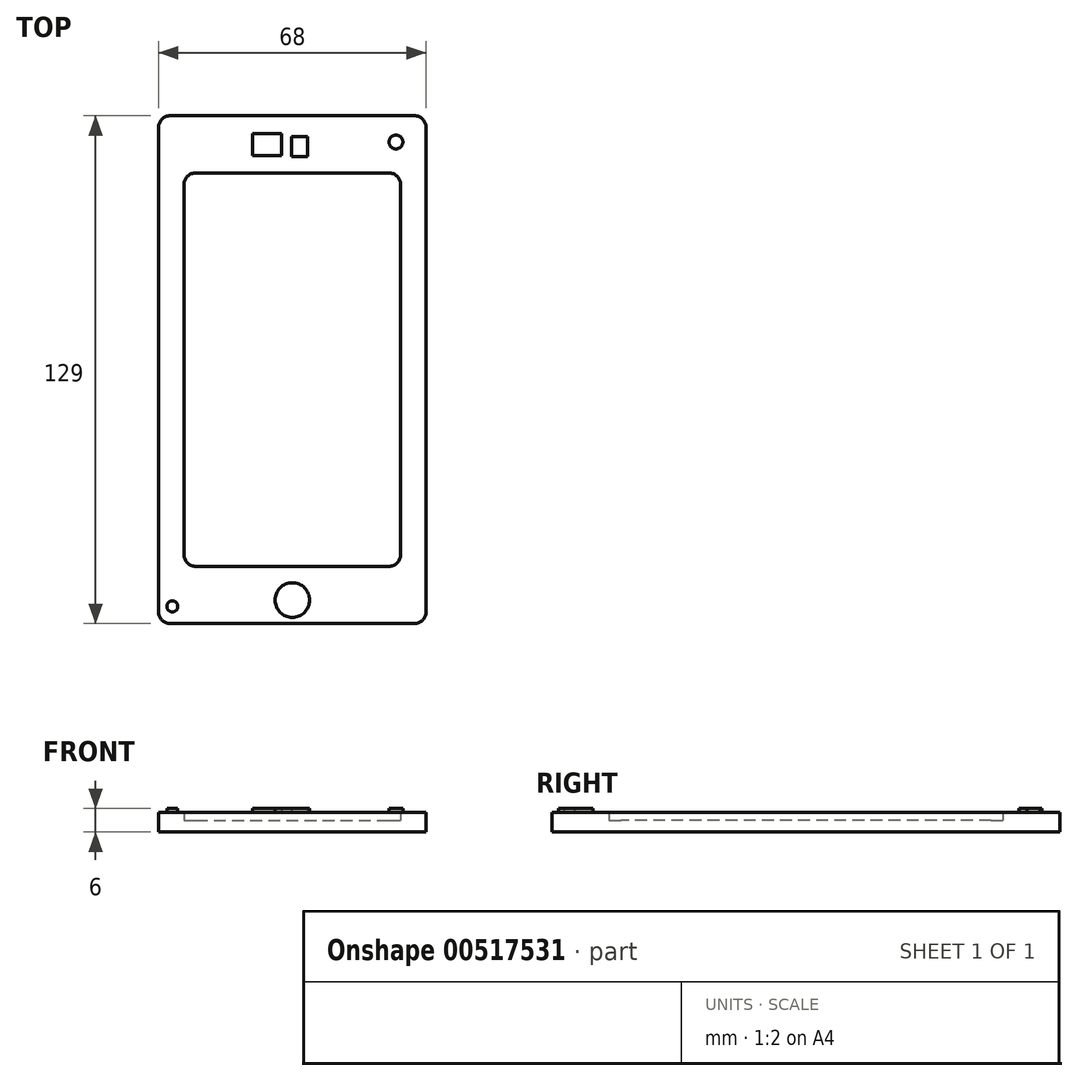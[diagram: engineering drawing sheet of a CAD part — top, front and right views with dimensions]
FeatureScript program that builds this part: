
annotation { "Feature Type Name" : "Feature", "Feature Type Description" : "" }
export const myFeature = defineFeature(function(context is Context, id is Id, definition is map)
    precondition{}
    {
        {
            var Q0;
            Q0=qCreatedBy(makeId("Top.planeOp"),FACE);
            var sketch = newSketch(context, id + "F0", { "sketchPlane" : qUnion([Q0])});
            skCircle(sketch, "E0", {"center": v(0, -58.54) * mm, "radius": 4.4 * mm});
            skSolve(sketch);
        }
        {
            var Q0;
            Q0=qCreatedBy(makeId("Top.planeOp"),FACE);
            var sketch = newSketch(context, id + "F1", { "sketchPlane" : qUnion([Q0])});
            skLineSegment(sketch, "E1.bottom", {"start": v(34, -64.5) * mm, "end": v(-34, -64.5) * mm});
            skLineSegment(sketch, "E1.top", {"start": v(34, 64.5) * mm, "end": v(-34, 64.5) * mm});
            skLineSegment(sketch, "E1.left", {"start": v(34, -64.5) * mm, "end": v(34, 64.5) * mm});
            skLineSegment(sketch, "E1.right", {"start": v(-34, -64.5) * mm, "end": v(-34, 64.5) * mm});
            skPoint(sketch, "E1.middle", {"position": v(0, 0) * mm});
            skLineSegment(sketch, "E2.bottom", {"start": v(-27.5, 50) * mm, "end": v(27.5, 50) * mm});
            skLineSegment(sketch, "E2.top", {"start": v(-27.5, -50) * mm, "end": v(27.5, -50) * mm});
            skLineSegment(sketch, "E2.left", {"start": v(-27.5, 50) * mm, "end": v(-27.5, -50) * mm});
            skLineSegment(sketch, "E2.right", {"start": v(27.5, 50) * mm, "end": v(27.5, -50) * mm});
            skSolve(sketch);
        }
        {
            var Q0;
            Q0=makeQuery(id+"F1.imprint","IMPRINT",FACE,{"disambiguationData":[TD([[makeQuery(id+"F1.imprint","IMPRINT",EDGE,{"derivedFrom":sQuery(id+"F1.wireOp",EDGE,"E1.bottom")}),-1.0]])]});
            extrude(context, id + "F2", {"entities" : qUnion([Q0]), "depth" : 5 * mm, "offsetDistance" : 25.4 * mm});
        }
        {
            var Q0;
            Q0=makeQuery(id+"F2.opExtrude","SWEPT_EDGE",EDGE,{"disambiguationData":[OSD([sQuery(id+"F1.wireOp",EDGE,"E1.top"),sQuery(id+"F1.wireOp",EDGE,"E1.right")])]});
            var Q1;
            Q1=makeQuery(id+"F2.opExtrude","SWEPT_EDGE",EDGE,{"disambiguationData":[OSD([sQuery(id+"F1.wireOp",EDGE,"E1.top"),sQuery(id+"F1.wireOp",EDGE,"E1.left")])]});
            var Q2;
            Q2=makeQuery(id+"F2.opExtrude","SWEPT_EDGE",EDGE,{"disambiguationData":[OSD([sQuery(id+"F1.wireOp",EDGE,"E1.bottom"),sQuery(id+"F1.wireOp",EDGE,"E1.left")])]});
            var Q3;
            Q3=makeQuery(id+"F2.opExtrude","SWEPT_EDGE",EDGE,{"disambiguationData":[OSD([sQuery(id+"F1.wireOp",EDGE,"E1.bottom"),sQuery(id+"F1.wireOp",EDGE,"E1.right")])]});
            fillet(context, id + "F3", {"entities" : qUnion([Q0, Q1, Q2, Q3]), "radius" : 3 * mm, "tangentPropagation" : true, "allowEdgeOverflow" : false});
        }
        {
            var Q0;
            Q0=makeQuery(id+"F2.opExtrude","SWEPT_EDGE",EDGE,{"disambiguationData":[OSD([sQuery(id+"F1.wireOp",EDGE,"E2.bottom"),sQuery(id+"F1.wireOp",EDGE,"E2.left")])]});
            var Q1;
            Q1=makeQuery(id+"F2.opExtrude","SWEPT_EDGE",EDGE,{"disambiguationData":[OSD([sQuery(id+"F1.wireOp",EDGE,"E2.bottom"),sQuery(id+"F1.wireOp",EDGE,"E2.right")])]});
            var Q2;
            Q2=makeQuery(id+"F2.opExtrude","SWEPT_EDGE",EDGE,{"disambiguationData":[OSD([sQuery(id+"F1.wireOp",EDGE,"E2.top"),sQuery(id+"F1.wireOp",EDGE,"E2.left")])]});
            var Q3;
            Q3=makeQuery(id+"F2.opExtrude","SWEPT_EDGE",EDGE,{"disambiguationData":[OSD([sQuery(id+"F1.wireOp",EDGE,"E2.top"),sQuery(id+"F1.wireOp",EDGE,"E2.right")])]});
            fillet(context, id + "F4", {"entities" : qUnion([Q0, Q1, Q2, Q3]), "radius" : 3 * mm, "tangentPropagation" : true, "allowEdgeOverflow" : false});
        }
        {
            var Q0;
            Q0=qCreatedBy(makeId("Top.planeOp"),FACE);
            var sketch = newSketch(context, id + "F5", { "sketchPlane" : qUnion([Q0])});
            skLineSegment(sketch, "E3.bottom", {"start": v(-27.5, 50) * mm, "end": v(27.5, 50) * mm});
            skLineSegment(sketch, "E3.top", {"start": v(-27.5, -50) * mm, "end": v(27.5, -50) * mm});
            skLineSegment(sketch, "E3.left", {"start": v(-27.5, 50) * mm, "end": v(-27.5, -50) * mm});
            skLineSegment(sketch, "E3.right", {"start": v(27.5, 50) * mm, "end": v(27.5, -50) * mm});
            skPoint(sketch, "E3.middle", {"position": v(0, 0) * mm});
            skSolve(sketch);
        }
        {
            var Q0;
            Q0 = qSketchRegion(id + "F5", true);
            extrude(context, id + "F6", {"entities" : qUnion([Q0]), "operationType" : NewBodyOperationType.ADD, "depth" : 3 * mm, "offsetDistance" : 25.4 * mm});
        }
        {
            var Q0;
            Q0 = qSketchRegion(id + "F0", true);
            extrude(context, id + "F7", {"entities" : qUnion([Q0]), "operationType" : NewBodyOperationType.ADD, "depth" : 6 * mm, "offsetDistance" : 25.4 * mm});
        }
        {
            var Q0;
            Q0=qCreatedBy(makeId("Top.planeOp"),FACE);
            var sketch = newSketch(context, id + "F8", { "sketchPlane" : qUnion([Q0])});
            skLineSegment(sketch, "E4.bottom", {"start": v(3.93, 54.15) * mm, "end": v(-0.23, 54.15) * mm});
            skLineSegment(sketch, "E4.top", {"start": v(3.93, 59.23) * mm, "end": v(-0.23, 59.23) * mm});
            skLineSegment(sketch, "E4.left", {"start": v(3.93, 54.15) * mm, "end": v(3.93, 59.23) * mm});
            skLineSegment(sketch, "E4.right", {"start": v(-0.23, 54.15) * mm, "end": v(-0.23, 59.23) * mm});
            skPoint(sketch, "E4.middle", {"position": v(1.85, 56.69) * mm});
            skSolve(sketch);
        }
        {
            var Q0;
            Q0 = qSketchRegion(id + "F8", true);
            extrude(context, id + "F9", {"entities" : qUnion([Q0]), "operationType" : NewBodyOperationType.ADD, "depth" : 6 * mm, "offsetDistance" : 25.4 * mm});
        }
        {
            var Q0;
            Q0=qCreatedBy(makeId("Top.planeOp"),FACE);
            var sketch = newSketch(context, id + "F10", { "sketchPlane" : qUnion([Q0])});
            skLineSegment(sketch, "E5.bottom", {"start": v(-2.77, 54.38) * mm, "end": v(-10.16, 54.38) * mm});
            skLineSegment(sketch, "E5.top", {"start": v(-2.77, 59.92) * mm, "end": v(-10.16, 59.92) * mm});
            skLineSegment(sketch, "E5.left", {"start": v(-2.77, 54.38) * mm, "end": v(-2.77, 59.92) * mm});
            skLineSegment(sketch, "E5.right", {"start": v(-10.16, 54.38) * mm, "end": v(-10.16, 59.92) * mm});
            skPoint(sketch, "E5.middle", {"position": v(-6.47, 57.15) * mm});
            skSolve(sketch);
        }
        {
            var Q0;
            Q0 = qSketchRegion(id + "F10", true);
            extrude(context, id + "F11", {"entities" : qUnion([Q0]), "operationType" : NewBodyOperationType.ADD, "depth" : 6 * mm, "offsetDistance" : 25.4 * mm});
        }
        {
            var Q0;
            Q0=qCreatedBy(makeId("Top.planeOp"),FACE);
            var sketch = newSketch(context, id + "F12", { "sketchPlane" : qUnion([Q0])});
            skCircle(sketch, "E6", {"center": v(26.32, 57.84) * mm, "radius": 1.76 * mm});
            skSolve(sketch);
        }
        {
            var Q0;
            Q0 = qSketchRegion(id + "F12", true);
            extrude(context, id + "F13", {"entities" : qUnion([Q0]), "operationType" : NewBodyOperationType.ADD, "depth" : 6 * mm, "offsetDistance" : 25.4 * mm});
        }
        {
            var Q0;
            Q0=qCreatedBy(makeId("Top.planeOp"),FACE);
            var sketch = newSketch(context, id + "F14", { "sketchPlane" : qUnion([Q0])});
            skLineSegment(sketch, "E7", {"start": v(-21.01, -56) * mm, "end": v(-15.47, -56) * mm});
            skSolve(sketch);
        }
        {
            var Q0;
            Q0=sQuery(id+"F14.wireOp",EDGE,"E7");
            extrude(context, id + "F15", {"bodyType" : ToolBodyType.SURFACE, "surfaceEntities" : qUnion([Q0]), "depth" : 6 * mm, "offsetDistance" : 25.4 * mm});
        }
        {
            var Q0;
            Q0=qCreatedBy(makeId("Top.planeOp"),FACE);
            var sketch = newSketch(context, id + "F16", { "sketchPlane" : qUnion([Q0])});
            skLineSegment(sketch, "E8", {"start": v(-20.09, -57.84) * mm, "end": v(-15.7, -57.84) * mm});
            skSolve(sketch);
        }
        {
            var Q0;
            Q0=sQuery(id+"F16.wireOp",EDGE,"E8");
            extrude(context, id + "F17", {"bodyType" : ToolBodyType.SURFACE, "surfaceEntities" : qUnion([Q0]), "depth" : 6 * mm, "offsetDistance" : 25.4 * mm});
        }
        {
            var Q0;
            Q0=qCreatedBy(makeId("Top.planeOp"),FACE);
            var sketch = newSketch(context, id + "F18", { "sketchPlane" : qUnion([Q0])});
            skLineSegment(sketch, "E9", {"start": v(-18.24, -59.7) * mm, "end": v(-15.7, -59.7) * mm});
            skSolve(sketch);
        }
        {
            var Q0;
            Q0 = qSketchRegion(id + "F18", true);
            var Q1;
            Q1=sQuery(id+"F18.wireOp",EDGE,"E9");
            extrude(context, id + "F19", {"entities" : qUnion([Q0]), "bodyType" : ToolBodyType.SURFACE, "surfaceEntities" : qUnion([Q1]), "depth" : 6 * mm, "offsetDistance" : 25.4 * mm});
        }
        {
            var Q0;
            Q0=qCreatedBy(makeId("Top.planeOp"),FACE);
            var sketch = newSketch(context, id + "F20", { "sketchPlane" : qUnion([Q0])});
            skLineSegment(sketch, "E10", {"start": v(17.55, -59.7) * mm, "end": v(24.48, -59.7) * mm});
            skLineSegment(sketch, "E11", {"start": v(24.48, -59.7) * mm, "end": v(24.48, -53) * mm});
            skLineSegment(sketch, "E12", {"start": v(24.48, -53) * mm, "end": v(17.78, -53) * mm});
            skLineSegment(sketch, "E13", {"start": v(17.78, -53) * mm, "end": v(17.78, -55.07) * mm});
            skLineSegment(sketch, "E14", {"start": v(17.78, -55.07) * mm, "end": v(14.32, -53) * mm});
            skLineSegment(sketch, "E15", {"start": v(14.32, -53) * mm, "end": v(17.78, -50.22) * mm});
            skLineSegment(sketch, "E16", {"start": v(17.78, -50.22) * mm, "end": v(17.78, -53) * mm});
            skSolve(sketch);
        }
        {
            var Q0;
            Q0 = qSketchRegion(id + "F20", true);
            var Q1;
            Q1=sQuery(id+"F20.wireOp",EDGE,"E15");
            var Q2;
            Q2=sQuery(id+"F20.wireOp",EDGE,"E16");
            var Q3;
            Q3=sQuery(id+"F20.wireOp",EDGE,"E14");
            var Q4;
            Q4=sQuery(id+"F20.wireOp",EDGE,"E13");
            extrude(context, id + "F21", {"entities" : qUnion([Q0]), "bodyType" : ToolBodyType.SURFACE, "surfaceEntities" : qUnion([Q1, Q2, Q3, Q4]), "depth" : 6 * mm, "offsetDistance" : 25.4 * mm});
        }
        {
            var Q0;
            Q0=qCreatedBy(makeId("Top.planeOp"),FACE);
            var sketch = newSketch(context, id + "F22", { "sketchPlane" : qUnion([Q0])});
            skLineSegment(sketch, "E17", {"start": v(17.78, -52.53) * mm, "end": v(21.24, -52.53) * mm});
            skLineSegment(sketch, "E18", {"start": v(21.24, -52.53) * mm, "end": v(21.24, -56.46) * mm});
            skLineSegment(sketch, "E19", {"start": v(21.24, -56.46) * mm, "end": v(16.86, -56.46) * mm});
            skSolve(sketch);
        }
        {
            var Q0;
            Q0 = qSketchRegion(id + "F22", true);
            var Q1;
            Q1=sQuery(id+"F22.wireOp",EDGE,"E17");
            var Q2;
            Q2=sQuery(id+"F22.wireOp",EDGE,"E18");
            var Q3;
            Q3=sQuery(id+"F22.wireOp",EDGE,"E19");
            extrude(context, id + "F23", {"entities" : qUnion([Q0]), "bodyType" : ToolBodyType.SURFACE, "surfaceEntities" : qUnion([Q1, Q2, Q3]), "depth" : 6 * mm, "offsetDistance" : 25.4 * mm});
        }
        {
            var Q0;
            Q0=qCreatedBy(makeId("Top.planeOp"),FACE);
            var sketch = newSketch(context, id + "F24", { "sketchPlane" : qUnion([Q0])});
            skCircle(sketch, "E20", {"center": v(-30.48, -60.15) * mm, "radius": 1.39 * mm});
            skSolve(sketch);
        }
        {
            var Q0;
            Q0 = qSketchRegion(id + "F24", true);
            extrude(context, id + "F25", {"entities" : qUnion([Q0]), "operationType" : NewBodyOperationType.ADD, "depth" : 6 * mm, "offsetDistance" : 25.4 * mm});
        }
    });
